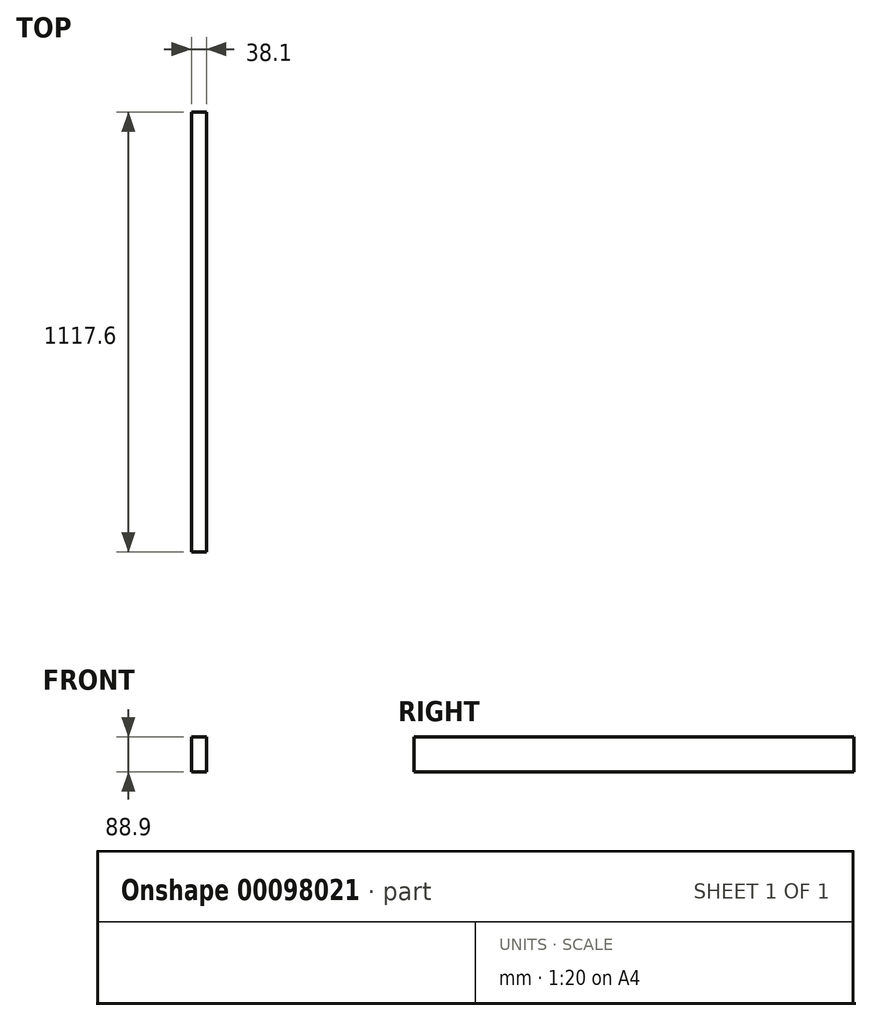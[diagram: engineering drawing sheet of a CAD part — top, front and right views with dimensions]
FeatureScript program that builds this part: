
annotation { "Feature Type Name" : "Feature", "Feature Type Description" : "" }
export const myFeature = defineFeature(function(context is Context, id is Id, definition is map)
    precondition{}
    {
        {
            var Q0;
            Q0=qCreatedBy(makeId("Right.planeOp"),FACE);
            var sketch = newSketch(context, id + "F0", { "sketchPlane" : qUnion([Q0])});
            skLineSegment(sketch, "E0.bottom", {"start": v(558.8, 44.45) * mm, "end": v(-558.8, 44.45) * mm});
            skLineSegment(sketch, "E0.top", {"start": v(558.8, -44.45) * mm, "end": v(-558.8, -44.45) * mm});
            skLineSegment(sketch, "E0.left", {"start": v(558.8, 44.45) * mm, "end": v(558.8, -44.45) * mm});
            skLineSegment(sketch, "E0.right", {"start": v(-558.8, 44.45) * mm, "end": v(-558.8, -44.45) * mm});
            skPoint(sketch, "E0.middle", {"position": v(0, 0) * mm});
            skSolve(sketch);
        }
        {
            var Q0;
            Q0=makeQuery(id+"F0.imprint","IMPRINT",FACE,{"disambiguationData":[TD([[makeQuery(id+"F0.imprint","IMPRINT",EDGE,{"derivedFrom":sQuery(id+"F0.wireOp",EDGE,"E0.bottom")}),1.0]])]});
            extrude(context, id + "F1", {"entities" : qUnion([Q0]), "depth" : 38.1 * mm});
        }
    });
